# Revit family: Legrand_Gestion_eclairage_Detecteur_Presence_Plafond_KNX
name_source: partatom
category: Dispositifs d'éclairage
units: mm (PartAtom-declared; Revit-internal decimal feet)

## family parameters
Conserver l'orientation des annotations = Non
Cote de connecteur circulaire = Utiliser le diamètre
Couper avec des vides une fois chargée = Non
Hôte = Face
Partagée = Non
Point de calcul de pièce = Non
Type d'élément = Normal

## types (3) — shared parameters
Adapté pour transmission sans fil = Non
Angle de détection horizontal (MAX) (°) = 360
Collecteur de terre = Non
Condition Générale d'Utilisation = https://export.legrand.com
Cosses d'artère secondaire = Non
Couleur = Blanc
Coupure forcée = Non
Durée d'enclenchement min. (s) = 5
Elévation par défaut = 1219 mm
Entrée secondaire = Non
Fabricant = Legrand
Fonction variateur intégré = Non
Gestion CVC = Non
Gestion alarme = Non
Hauteur de montage maximale (m) = 2.5
Liaison neutre = Non
Numéro RAL = 9003
Réglage de lumière constante = Oui
Sensibilité lumineuse réglable = Oui
Sensibilité réglable = Oui
Télécommandable = Non
URL = http://www.legrandoc.com
zero-valued in all types: Capacité de coupure max. (W), Courant de démarrage max. (A), Fréquence (MAX) (Hz), Fréquence (MIN) (Hz), Sensibilité lumineuse (MAX) (lx), Sensibilité lumineuse (MIN) (lx), Température (MAX) (°C), Température (MIN) (°C), Tension nominale (V)

## per-type parameters (varying)
| type | Angle de détection horizontal (MIN) (°) | Description | Diamètre de détection sur le plancher (m) | Dual-tech KNX faux-plafond 360° | Durée d'enclenchement max. (mn) | Exécution - Modèle | KNX PIR High density | Mode de montage | Modèle | PIR KNX faux-plafond 2x180° | Portée max. frontale (m) | Portée max. latérale (m) |
| PIR KNX faux-plafond 2x180° | 0 | Détecteur de mouvement BUS/KNX - spécial couloir - fixation plafond - 2 x 12 m | 3 | Non | 18 | détecteur de mouvement | Non | encastré | 048919 | Oui | 0 | 12 |
| KNX PIR High density | 360 | Détecteur de présence BUS/KNX - IP20 - IR - fixation plafond - Ø 8 m | 8 | Non | 1080 | détecteur de présence | Oui | apparent | 048922 | Non | 4 | 4 |
| Dual-tech KNX faux-plafond 360° | 0 | Détecteur de présence BUS/KNX - fixation plafond - Ø 8 m | 8 | Oui | 18 | détecteur de mouvement | Non | encastré | 048918 | Non | 0 | 4 |
